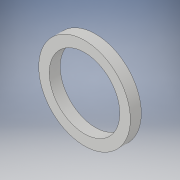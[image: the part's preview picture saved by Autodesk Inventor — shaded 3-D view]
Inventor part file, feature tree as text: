
AUTODESK INVENTOR PART (.ipt)
format: ipt  version: 2019 (Build 230136000, 136)  size: 103,936 bytes
history: native  units: mm
features: extrude x2, sketch x2
ambient origin geometry x8: Origin, YZ Plane, XZ Plane, XY Plane, X Axis, Y Axis, Z Axis, Center Point
bodies: Solid1 (feature_tree)
feature tree (4):
  extrude  "Extrusion1"  Depth=41.1mm TaperAngle=0.0deg
  extrude  "Extrusion2"  Depth=4.11mm TaperAngle=0.0deg
  sketch  "Sketch1"  dims[d0=344.0mm d1=41.1mm d2=0.0mm]
  sketch  "Sketch2"  dims[d3=265.0mm d4=4.11mm d5=0.0mm]
